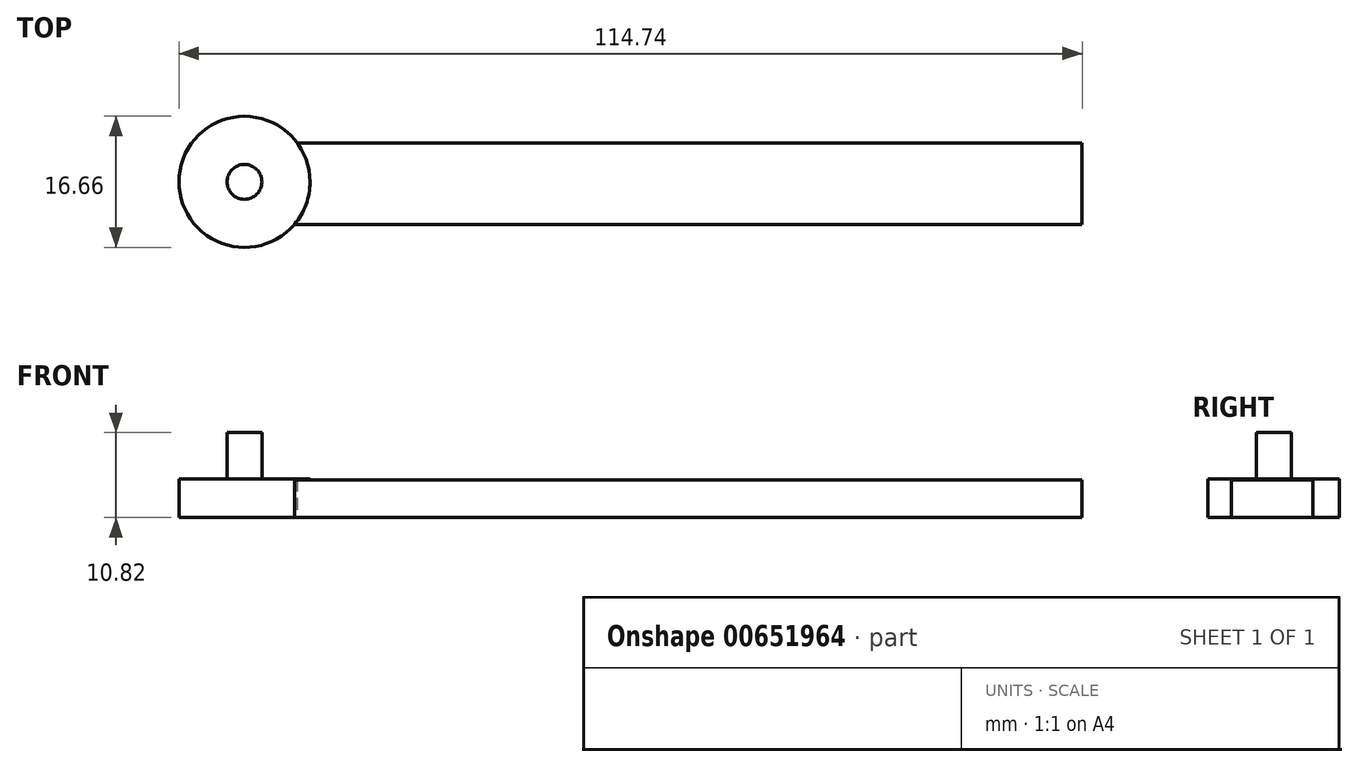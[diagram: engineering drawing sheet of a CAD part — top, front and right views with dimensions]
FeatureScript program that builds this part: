
annotation { "Feature Type Name" : "Feature", "Feature Type Description" : "" }
export const myFeature = defineFeature(function(context is Context, id is Id, definition is map)
    precondition{}
    {
        {
            var Q0;
            Q0=qCreatedBy(makeId("Top.planeOp"),FACE);
            var sketch = newSketch(context, id + "F0", { "sketchPlane" : qUnion([Q0])});
            skLineSegment(sketch, "E0.bottom", {"start": v(-38.9, 18.62) * mm, "end": v(64.83, 18.62) * mm});
            skLineSegment(sketch, "E0.top", {"start": v(-38.9, 28.98) * mm, "end": v(64.83, 28.98) * mm});
            skLineSegment(sketch, "E0.left", {"start": v(-38.9, 18.62) * mm, "end": v(-38.9, 28.98) * mm});
            skLineSegment(sketch, "E0.right", {"start": v(64.83, 18.62) * mm, "end": v(64.83, 28.98) * mm});
            skSolve(sketch);
        }
        {
            var Q0;
            Q0 = qSketchRegion(id + "F0", true);
            extrude(context, id + "F1", {"entities" : qUnion([Q0]), "depth" : 4.8 * mm, "offsetDistance" : 25.4 * mm});
        }
        {
            var Q0;
            Q0=qCreatedBy(makeId("Top.planeOp"),FACE);
            var sketch = newSketch(context, id + "F2", { "sketchPlane" : qUnion([Q0])});
            skCircle(sketch, "E1", {"center": v(-41.58, 24.03) * mm, "radius": 8.33 * mm});
            skSolve(sketch);
        }
        {
            var Q0;
            Q0 = qSketchRegion(id + "F2", true);
            extrude(context, id + "F3", {"entities" : qUnion([Q0]), "operationType" : NewBodyOperationType.ADD, "depth" : 4.93 * mm, "offsetDistance" : 25.4 * mm});
        }
        {
            var Q0;
            Q0=makeQuery(id+"F3.opExtrude","CAP_FACE",FACE,{"disambiguationData":[OSD([sQuery(id+"F2.wireOp",EDGE,"E1")])],"isStart":false});
            var sketch = newSketch(context, id + "F4", { "sketchPlane" : qUnion([Q0])});
            skCircle(sketch, "E2", {"center": v(-41.58, 24.03) * mm, "radius": 2.22 * mm});
            skSolve(sketch);
        }
        {
            var Q0;
            Q0 = qSketchRegion(id + "F4", true);
            extrude(context, id + "F5", {"entities" : qUnion([Q0]), "operationType" : NewBodyOperationType.ADD, "depth" : 5.89 * mm, "offsetDistance" : 25.4 * mm});
        }
    });
